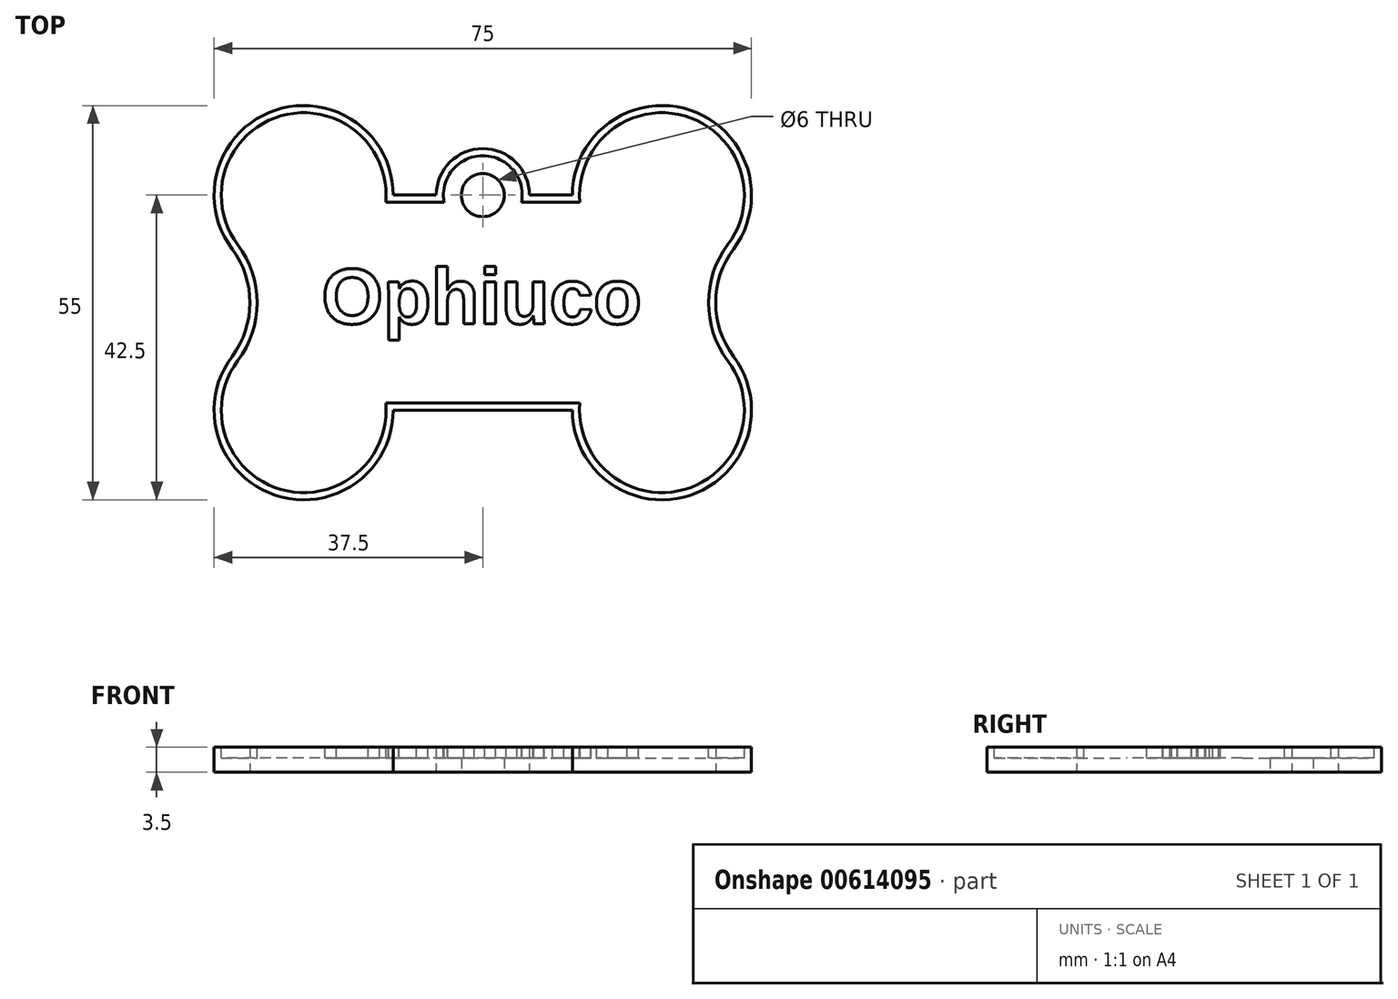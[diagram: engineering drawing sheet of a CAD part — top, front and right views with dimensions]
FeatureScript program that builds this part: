
annotation { "Feature Type Name" : "Feature", "Feature Type Description" : "" }
export const myFeature = defineFeature(function(context is Context, id is Id, definition is map)
    precondition{}
    {
        {
            var Q0;
            Q0=qCreatedBy(makeId("Top.planeOp"),FACE);
            var sketch = newSketch(context, id + "F0", { "sketchPlane" : qUnion([Q0])});
            skArc(sketch, "E0", {"start": v(22.5, 30) * mm, "mid": v(6.05, 41.86) * mm, "end": v(0, 22.5) * mm});
            skArc(sketch, "E1", {"start": v(0, 7.5) * mm, "mid": v(6.05, -11.86) * mm, "end": v(22.5, 0) * mm});
            skArc(sketch, "E2", {"start": v(47.5, 0) * mm, "mid": v(63.95, -11.86) * mm, "end": v(70, 7.5) * mm});
            skArc(sketch, "E3", {"start": v(70, 22.5) * mm, "mid": v(63.95, 41.86) * mm, "end": v(47.5, 30) * mm});
            skArc(sketch, "E4", {"start": v(0, 7.5) * mm, "mid": v(2.5, 15) * mm, "end": v(0, 22.5) * mm});
            skPoint(sketch, "E4.first.point", {"position": v(0, 22.5) * mm});
            skPoint(sketch, "E4.second.point", {"position": v(0, 7.5) * mm});
            skPoint(sketch, "E4.third.point", {"position": v(-22.5, 15) * mm});
            skPoint(sketch, "E4.third.point.positionSnap0", {"position": v(0, 15) * mm});
            skArc(sketch, "E5", {"start": v(70, 22.5) * mm, "mid": v(67.5, 15) * mm, "end": v(70, 7.5) * mm});
            skPoint(sketch, "E5.first.point", {"position": v(70, 22.5) * mm});
            skPoint(sketch, "E5.second.point", {"position": v(70, 7.5) * mm});
            skPoint(sketch, "E5.third.point", {"position": v(92.23, 12.43) * mm});
            skLineSegment(sketch, "E6.trimOffspring", {"start": v(22.5, 0) * mm, "end": v(47.5, 0) * mm});
            skPoint(sketch, "E7.orphan", {"position": v(0, 30) * mm});
            skPoint(sketch, "E8.start.orphan", {"position": v(0, 0) * mm});
            skLineSegment(sketch, "E9.trimOffspring", {"start": v(47.5, 30) * mm, "end": v(41.5, 30) * mm});
            skLineSegment(sketch, "E10", {"start": v(22.5, 30) * mm, "end": v(28.5, 30) * mm, "construction": true});
            skArc(sketch, "E11", {"start": v(41.5, 30) * mm, "mid": v(35, 36.5) * mm, "end": v(28.5, 30) * mm});
            skCircle(sketch, "E12", {"center": v(35, 30) * mm, "radius": 3 * mm});
            skLineSegment(sketch, "E13.trimOffspring", {"start": v(28.5, 30) * mm, "end": v(22.5, 30) * mm});
            skSolve(sketch);
        }
        {
            var Q0;
            Q0 = qSketchRegion(id + "F0", true);
            extrude(context, id + "F1", {"entities" : qUnion([Q0]), "depth" : 3.5 * mm, "offsetDistance" : 25 * mm});
        }
        {
            var Q0;
            Q0=makeQuery(id+"F1.opExtrude","CAP_FACE",FACE,{"disambiguationData":[OSD([sQuery(id+"F0.wireOp",EDGE,"E0"),sQuery(id+"F0.wireOp",EDGE,"E1"),sQuery(id+"F0.wireOp",EDGE,"E2"),sQuery(id+"F0.wireOp",EDGE,"E3"),sQuery(id+"F0.wireOp",EDGE,"E4"),sQuery(id+"F0.wireOp",EDGE,"E5"),sQuery(id+"F0.wireOp",EDGE,"E6.trimOffspring"),sQuery(id+"F0.wireOp",EDGE,"E9.trimOffspring"),sQuery(id+"F0.wireOp",EDGE,"E11"),sQuery(id+"F0.wireOp",EDGE,"E12"),sQuery(id+"F0.wireOp",EDGE,"E13.trimOffspring")])],"isStart":false});
            var sketch = newSketch(context, id + "F2", { "sketchPlane" : qUnion([Q0])});
            skText(sketch, "E14", { "text": "Ophiuco", "fontName": "Arimo-Bold.ttf"});
            skArc(sketch, "E15.0", {"start": v(48.54, 1) * mm, "mid": v(63.16, -11.06) * mm, "end": v(69.2, 6.9) * mm});
            skLineSegment(sketch, "E15.1", {"start": v(21.46, 1) * mm, "end": v(48.54, 1) * mm});
            skArc(sketch, "E15.2", {"start": v(69.2, 6.9) * mm, "mid": v(66.5, 15) * mm, "end": v(69.2, 23.1) * mm});
            skArc(sketch, "E15.3", {"start": v(0.8, 6.9) * mm, "mid": v(6.84, -11.06) * mm, "end": v(21.46, 1) * mm});
            skArc(sketch, "E15.4", {"start": v(0.8, 23.1) * mm, "mid": v(3.5, 15) * mm, "end": v(0.8, 6.9) * mm});
            skArc(sketch, "E15.5", {"start": v(21.46, 29) * mm, "mid": v(6.84, 41.06) * mm, "end": v(0.8, 23.1) * mm});
            skArc(sketch, "E15.6", {"start": v(69.2, 23.1) * mm, "mid": v(63.16, 41.06) * mm, "end": v(48.54, 29) * mm});
            skLineSegment(sketch, "E15.7", {"start": v(48.54, 29) * mm, "end": v(40.4, 29) * mm});
            skArc(sketch, "E15.8", {"start": v(40.4, 29) * mm, "mid": v(35, 35.5) * mm, "end": v(29.6, 29) * mm});
            skLineSegment(sketch, "E15.9", {"start": v(29.6, 29) * mm, "end": v(21.46, 29) * mm});
            const initialGuessF2  = {"E14": [0.0125, 0.01207, 1, 0, 0.00793]};
            skSetInitialGuess(sketch, initialGuessF2);
            skSolve(sketch);
        }
        {
            var Q0;
            Q0 = qSketchRegion(id + "F2", true);
            var Q1;
            Q1=makeQuery(id+"F2.imprint","IMPRINT",FACE,{"disambiguationData":[TD([[makeQuery(id+"F2.imprint","IMPRINT",EDGE,{"derivedFrom":sQuery(id+"F2.wireOp",EDGE,"E14.sketch_text.stroke-9")}),1.0]])]});
            var Q2;
            Q2=makeQuery(id+"F2.imprint","IMPRINT",FACE,{"disambiguationData":[TD([[makeQuery(id+"F2.imprint","IMPRINT",EDGE,{"derivedFrom":sQuery(id+"F2.wireOp",EDGE,"E14.sketch_text.stroke-34")}),1.0]])]});
            var Q3;
            Q3=makeQuery(id+"F2.imprint","IMPRINT",FACE,{"disambiguationData":[TD([[makeQuery(id+"F2.imprint","IMPRINT",EDGE,{"derivedFrom":sQuery(id+"F2.wireOp",EDGE,"E14.sketch_text.stroke-107")}),1.0]])]});
            extrude(context, id + "F3", {"entities" : qUnion([Q0, Q1, Q2, Q3]), "operationType" : NewBodyOperationType.REMOVE, "oppositeDirection" : true, "depth" : 1.5 * mm, "offsetDistance" : 25 * mm});
        }
    });
